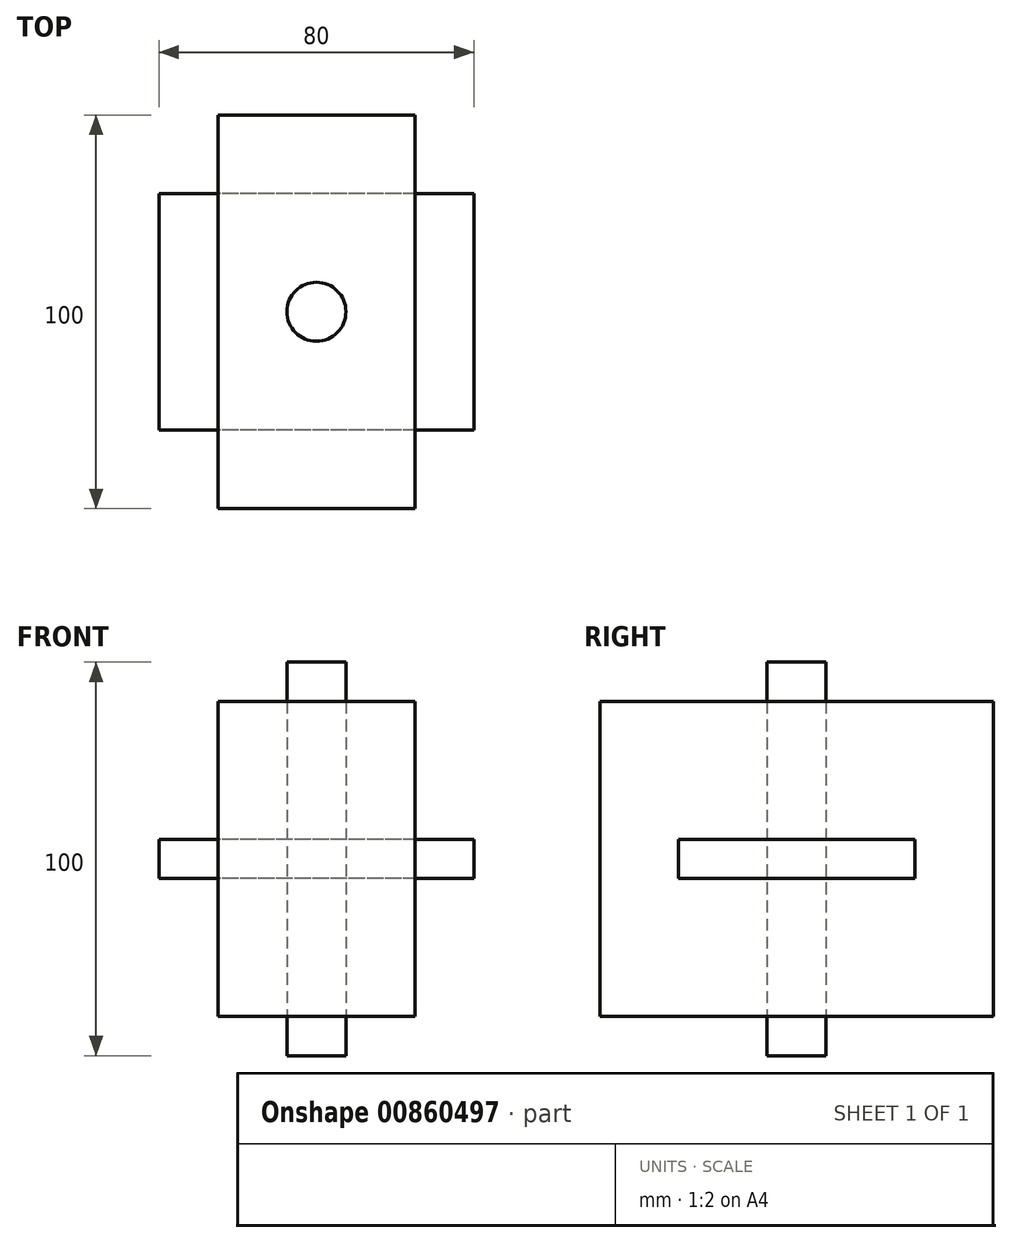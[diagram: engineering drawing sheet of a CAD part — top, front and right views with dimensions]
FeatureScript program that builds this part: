
annotation { "Feature Type Name" : "Feature", "Feature Type Description" : "" }
export const myFeature = defineFeature(function(context is Context, id is Id, definition is map)
    precondition{}
    {
        {
            var Q0;
            Q0=qCreatedBy(makeId("Top.planeOp"),FACE);
            var sketch = newSketch(context, id + "F0", { "sketchPlane" : qUnion([Q0])});
            skLineSegment(sketch, "E0.bottom", {"start": v(-25, 50) * mm, "end": v(25, 50) * mm});
            skLineSegment(sketch, "E0.top", {"start": v(-25, -50) * mm, "end": v(25, -50) * mm});
            skLineSegment(sketch, "E0.left", {"start": v(-25, 50) * mm, "end": v(-25, -50) * mm});
            skLineSegment(sketch, "E0.right", {"start": v(25, 50) * mm, "end": v(25, -50) * mm});
            skPoint(sketch, "E0.middle", {"position": v(0, 0) * mm});
            skSolve(sketch);
        }
        {
            var Q0;
            Q0 = qSketchRegion(id + "F0", true);
            extrude(context, id + "F1", {"entities" : qUnion([Q0]), "depth" : 80 * mm, "offsetDistance" : 25 * mm, "symmetric" : true});
        }
        {
            var Q0;
            Q0=qCreatedBy(makeId("Top.planeOp"),FACE);
            var sketch = newSketch(context, id + "F2", { "sketchPlane" : qUnion([Q0])});
            skCircle(sketch, "E1", {"center": v(0, 0) * mm, "radius": 7.5 * mm});
            skSolve(sketch);
        }
        {
            var Q0;
            Q0 = qSketchRegion(id + "F2", true);
            extrude(context, id + "F3", {"entities" : qUnion([Q0]), "depth" : 100 * mm, "offsetDistance" : 25 * mm, "symmetric" : true});
        }
        {
            var Q0;
            Q0=qCreatedBy(makeId("Top.planeOp"),FACE);
            var sketch = newSketch(context, id + "F4", { "sketchPlane" : qUnion([Q0])});
            skCircle(sketch, "E2", {"center": v(0, 0) * mm, "radius": 7.5 * mm});
            skSolve(sketch);
        }
        {
            var Q0;
            Q0 = qSketchRegion(id + "F4", true);
            extrude(context, id + "F5", {"entities" : qUnion([Q0]), "depth" : 100 * mm, "offsetDistance" : 25 * mm, "symmetric" : true});
        }
        {
            var Q0;
            Q0=qCreatedBy(makeId("Top.planeOp"),FACE);
            var sketch = newSketch(context, id + "F6", { "sketchPlane" : qUnion([Q0])});
            skLineSegment(sketch, "E3.bottom", {"start": v(40, 30) * mm, "end": v(-40, 30) * mm});
            skLineSegment(sketch, "E3.top", {"start": v(40, -30) * mm, "end": v(-40, -30) * mm});
            skLineSegment(sketch, "E3.left", {"start": v(40, 30) * mm, "end": v(40, -30) * mm});
            skLineSegment(sketch, "E3.right", {"start": v(-40, 30) * mm, "end": v(-40, -30) * mm});
            skPoint(sketch, "E3.middle", {"position": v(0, 0) * mm});
            skSolve(sketch);
        }
        {
            var Q0;
            Q0=makeQuery(id+"F6.imprint","IMPRINT",FACE,{"disambiguationData":[TD([[makeQuery(id+"F6.imprint","IMPRINT",EDGE,{"derivedFrom":sQuery(id+"F6.wireOp",EDGE,"E3.bottom")}),1.0]])]});
            extrude(context, id + "F7", {"entities" : qUnion([Q0]), "depth" : 10 * mm, "offsetDistance" : 25 * mm, "symmetric" : true});
        }
    });
